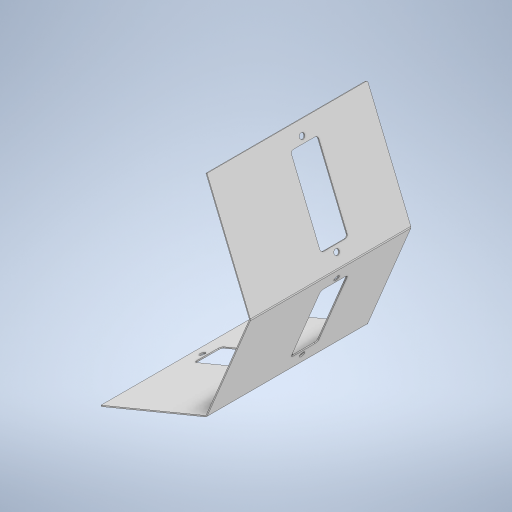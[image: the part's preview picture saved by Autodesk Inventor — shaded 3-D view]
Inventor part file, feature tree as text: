
AUTODESK INVENTOR PART (.ipt)
format: ipt  version: 2024.2 (Build 282272000, 272)  size: 500,224 bytes
history: native  units: mm
features: sheet_metal_op x3, other x3, sketch x3, extrude x2, fillet x1, pattern_circular x1, pattern_linear x1
ambient origin geometry x8: Origin, YZ Plane, XZ Plane, XY Plane, X Axis, Y Axis, Z Axis, Center Point
bodies: Body1 (feature_tree)
feature tree (14):
  sheet_metal_op  "Contour Flange2"
  extrude  "Extrusion4"  Depth=2.0mm
  fillet  "Fillet1"  Radius=1.0mm
  pattern_circular  "Circular Pattern1"  [2 undecoded]
  pattern_linear  "Rectangular Pattern2"  Spacing1=2.0mm  [1 undecoded]
  other  "Corner Chamfer1"
  extrude  "Extrusion5"  Depth=2.0mm
  sketch  "Sketch2"  dims[d25=2.0mm d26=2.0mm d27=1.0mm]
  other  "Plate2"
  sheet_metal_op  "Bend2"
  sheet_metal_op  "Corner2"
  sketch  "Sketch10"  dims[d28=4.0mm]
  sketch  "Sketch11"  dims[d29=2.0mm d30=2006.0mm d31=2.0mm d32=3.0mm d33=8.0mm d34=2.0mm d35=2.0mm d56=506.0mm d58=4.0mm d69=0.9mm d70=4.0mm d71=0.9mm d107=145.0mm d108=50.0mm d109=10.0mm d110=10.0mm d112=0.0mm d113=0.0mm d114=5.0mm d115=30.0mm d116=90.0deg d118=125.0mm d119=80.0mm d121=250.0mm d122=2.0mm d123=6.0mm d124=45.0deg d125=600.0mm d126=1712.25mm d127=600.0mm d128=0.0mm]
  other  "Definition1"
note: 3 required parameter values undecoded (feature->parameter linkage not recoverable at this tier; creation-order binding heuristic only, values carry confidence <= 0.55)
